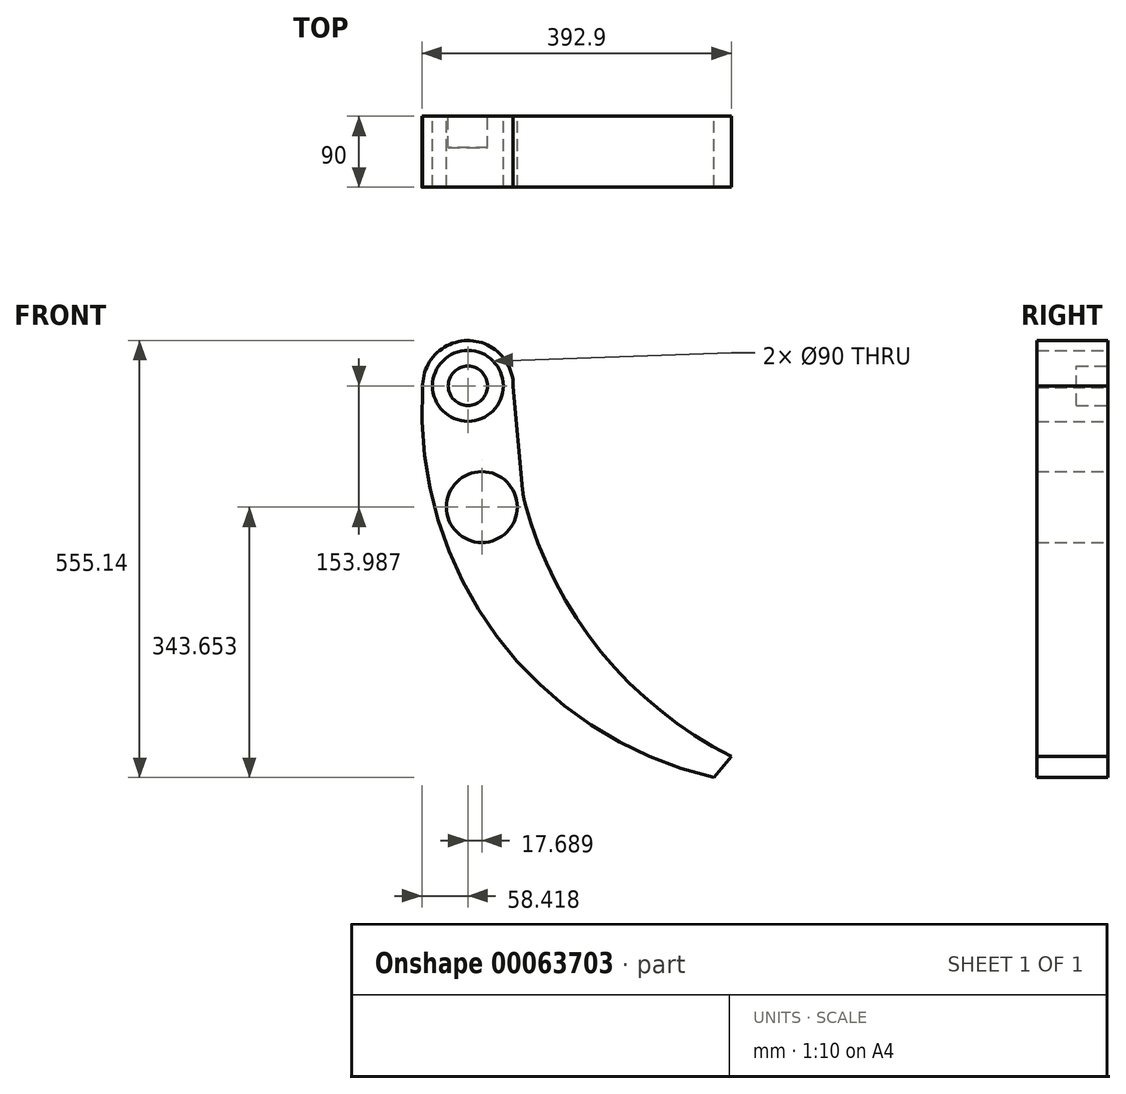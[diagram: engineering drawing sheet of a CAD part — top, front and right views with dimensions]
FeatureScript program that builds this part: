
annotation { "Feature Type Name" : "Feature", "Feature Type Description" : "" }
export const myFeature = defineFeature(function(context is Context, id is Id, definition is map)
    precondition{}
    {
        {
            var Q0;
            Q0=qCreatedBy(makeId("Front.planeOp"),FACE);
            var sketch = newSketch(context, id + "F0", { "sketchPlane" : qUnion([Q0])});
            skCircle(sketch, "E0", {"center": v(312.22, 941.06) * mm, "radius": 25 * mm});
            skLineSegment(sketch, "E1", {"start": v(381.65, 808.84) * mm, "end": v(369.72, 941.06) * mm});
            skArc(sketch, "E2", {"start": v(254.75, 939.09) * mm, "mid": v(348.7, 623.2) * mm, "end": v(624.93, 443.42) * mm});
            skArc(sketch, "E3", {"start": v(384.7, 791.8) * mm, "mid": v(481.4, 603.14) * mm, "end": v(646.7, 470.41) * mm});
            skLineSegment(sketch, "E4", {"start": v(646.7, 470.41) * mm, "end": v(624.93, 443.42) * mm});
            skCircle(sketch, "E5", {"center": v(329.9, 787.07) * mm, "radius": 20 * mm});
            skCircle(sketch, "E6", {"center": v(312.22, 941.06) * mm, "radius": 45 * mm});
            skCircle(sketch, "E7", {"center": v(329.9, 787.07) * mm, "radius": 45 * mm});
            skCircle(sketch, "E8", {"center": v(312.22, 941.06) * mm, "radius": 27.5 * mm});
            skArc(sketch, "E9", {"start": v(369.72, 941.06) * mm, "mid": v(311.23, 998.55) * mm, "end": v(254.75, 939.09) * mm});
            skArc(sketch, "E10", {"start": v(381.65, 808.84) * mm, "mid": v(382.8, 800.25) * mm, "end": v(384.7, 791.8) * mm});
            skSolve(sketch);
        }
        {
            var Q0;
            Q0=makeQuery(id+"F0.imprint","IMPRINT",FACE,{"disambiguationData":[TD([[makeQuery(id+"F0.imprint","IMPRINT",EDGE,{"derivedFrom":sQuery(id+"F0.wireOp",EDGE,"E1")}),1.0]])]});
            extrude(context, id + "F1", {"entities" : qUnion([Q0]), "depth" : 15 * mm});
        }
        {
            var Q0;
            Q0=makeQuery(id+"F0.imprint","IMPRINT",FACE,{"disambiguationData":[TD([[makeQuery(id+"F0.imprint","IMPRINT",EDGE,{"derivedFrom":sQuery(id+"F0.wireOp",EDGE,"E0")}),1.0]])]});
            extrude(context, id + "F2", {"entities" : qUnion([Q0]), "depth" : 40 * mm});
        }
        {
            var Q0;
            Q0=makeQuery(id+"F0.imprint","IMPRINT",FACE,{"disambiguationData":[TD([[makeQuery(id+"F0.imprint","IMPRINT",EDGE,{"derivedFrom":sQuery(id+"F0.wireOp",EDGE,"E6")}),-1.0]])]});
            extrude(context, id + "F3", {"entities" : qUnion([Q0]), "operationType" : NewBodyOperationType.ADD, "depth" : 90 * mm});
        }
    });
